# Revit family: PRD_AR_ShwrFttngsPckg_Anti-twistProtection_ZAQUA004
name_source: partatom
category: Specialty Equipment
revit_build: Autodesk Revit 2018 (Build: 20190510_1515(x64)
units: mm (PartAtom-declared; Revit-internal decimal feet)

## family parameters
Always vertical = Yes
Cut with Voids When Loaded = No
OmniClass Number = 23.45.05.14.99
OmniClass Title = Other Sanitary Washing Plumbing Fixtures
Part Type = Normal
Room Calculation Point = No
Round Connector Dimension = Use Diameter
Shared = Yes
Work Plane-Based = Yes

## types (1)
- ZAQUA004
    AssetType = Fixed
    BIMObjectName = PRD_AR_ShowerFittingsPackage_Anti-twistProtection_ZAQUA004
    BodyMaterial = PRD_AR_Steel
    Category = Pr_40_20_87_75, Shower fittings package
    Default Elevation = 1219 mm
    Description = Twist-proof set for shower head DN 15 AQUAJET-Slimline / AQUAJET-Comfort.
    DurationUnit = year
    Features = for shower head DN 15 AQUAJET-Slimline / AQUAJET-Comfort
    GrossWeight = 0.02 kg
    IfcExportAs = IfcSanitaryTerminalType
    IfcExportType = USERDEFINED
    Manufacturer = KWC Group AG
    ManufacturerName = KWC Group AG
    ManufacturerURL = www.kwc.com
    Model = ZAQUA004
    ModelNumber = 2000101108
    ModelReference = ZAQUA004
    NBSDescription = Shower fittings package
    NBSReference = 45-35-70/330
    Name = Anti-twist protection ZAQUA004
    NetWeight = 0.00 kg
    NominalDepth = 0 mm  [stored 0 ft]
    NominalHeight = 30 mm  [stored 0.0984252 ft]
    NominalLength = 0 mm  [stored 0 ft]
    NominalWidth = 0 mm  [stored 0 ft]
    ProductCode = 210.0574.630
    ProductInformation = https://pim.kwc.com
    Quantity = 1
    QuantityUom = Piece
    Status = New
    URL = www.kwc.com
    Uniclass2015Code = Pr_40_20_87_75
    Uniclass2015Title = Shower fittings package
    Uniclass2015Version = Products v1.17
    Version = 1
    WarrantyDurationUnit = year

note: [stored X ft] marks values corroborated as IEEE doubles in the binary element streams (Revit-internal decimal feet)

## geometry (parser evidence)
native form markers: Sweep x3
no freeform markers — native parametric forms only
